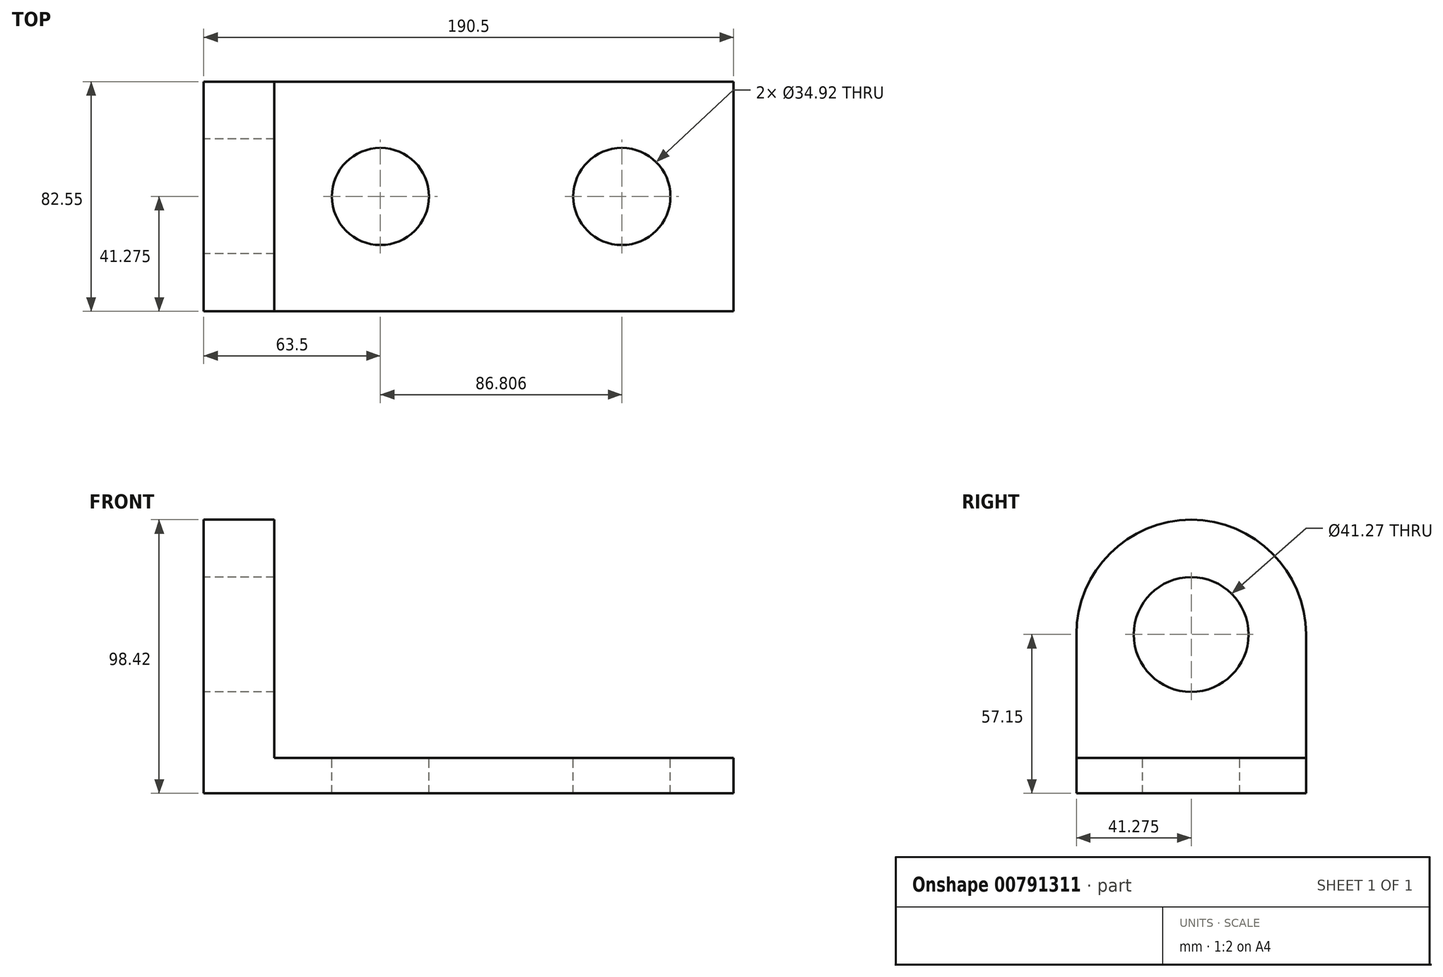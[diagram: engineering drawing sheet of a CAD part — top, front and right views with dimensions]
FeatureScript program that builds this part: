
annotation { "Feature Type Name" : "Feature", "Feature Type Description" : "" }
export const myFeature = defineFeature(function(context is Context, id is Id, definition is map)
    precondition{}
    {
        {
            var Q0;
            Q0=qCreatedBy(makeId("Front.planeOp"),FACE);
            var sketch = newSketch(context, id + "F0", { "sketchPlane" : qUnion([Q0])});
            skLineSegment(sketch, "E0", {"start": v(0, 0) * mm, "end": v(190.5, 0) * mm});
            skLineSegment(sketch, "E1", {"start": v(190.5, 0) * mm, "end": v(190.5, 12.7) * mm});
            skLineSegment(sketch, "E2", {"start": v(190.5, 12.7) * mm, "end": v(25.4, 12.7) * mm});
            skLineSegment(sketch, "E3", {"start": v(0, 0) * mm, "end": v(0, 107.95) * mm});
            skLineSegment(sketch, "E4", {"start": v(0, 107.95) * mm, "end": v(25.4, 107.95) * mm});
            skLineSegment(sketch, "E5", {"start": v(25.4, 12.7) * mm, "end": v(25.4, 107.95) * mm});
            skSolve(sketch);
        }
        {
            var Q0;
            Q0=makeQuery(id+"F0.imprint","IMPRINT",FACE,{"disambiguationData":[TD([[makeQuery(id+"F0.imprint","IMPRINT",EDGE,{"derivedFrom":sQuery(id+"F0.wireOp",EDGE,"E0")}),1.0]])]});
            extrude(context, id + "F1", {"entities" : qUnion([Q0]), "depth" : 82.55 * mm, "offsetDistance" : 25.4 * mm});
        }
        {
            var Q0;
            Q0=makeQuery(id+"F1.opExtrude","SWEPT_FACE",FACE,{"disambiguationData":[OSD([sQuery(id+"F0.wireOp",EDGE,"E2")])]});
            var sketch = newSketch(context, id + "F2", { "sketchPlane" : qUnion([Q0])});
            skLineSegment(sketch, "E6", {"start": v(25.4, -41.28) * mm, "end": v(63.5, -41.28) * mm, "construction": true});
            skLineSegment(sketch, "E7", {"start": v(63.5, -41.28) * mm, "end": v(150.3, -41.28) * mm, "construction": true});
            skCircle(sketch, "E8", {"center": v(63.5, -41.28) * mm, "radius": 17.46 * mm});
            skCircle(sketch, "E9", {"center": v(150.3, -41.28) * mm, "radius": 17.46 * mm});
            skSolve(sketch);
        }
        {
            var Q0;
            Q0=makeQuery(id+"F2.imprint","IMPRINT",FACE,{"disambiguationData":[TD([[makeQuery(id+"F2.imprint","IMPRINT",EDGE,{"derivedFrom":sQuery(id+"F2.wireOp",EDGE,"E8")}),1.0]])]});
            var Q1;
            Q1=makeQuery(id+"F2.imprint","IMPRINT",FACE,{"disambiguationData":[TD([[makeQuery(id+"F2.imprint","IMPRINT",EDGE,{"derivedFrom":sQuery(id+"F2.wireOp",EDGE,"E9")}),1.0]])]});
            extrude(context, id + "F3", {"entities" : qUnion([Q0, Q1]), "operationType" : NewBodyOperationType.REMOVE, "oppositeDirection" : true, "depth" : 25.4 * mm, "offsetDistance" : 25.4 * mm});
        }
        {
            var Q0;
            Q0=makeQuery(id+"F1.opExtrude","SWEPT_FACE",FACE,{"disambiguationData":[OSD([sQuery(id+"F0.wireOp",EDGE,"E3")])]});
            var sketch = newSketch(context, id + "F4", { "sketchPlane" : qUnion([Q0])});
            skLineSegment(sketch, "E10", {"start": v(0, 0) * mm, "end": v(0, 57.15) * mm, "construction": true});
            skLineSegment(sketch, "E11", {"start": v(82.55, 0) * mm, "end": v(82.55, 57.15) * mm, "construction": true});
            skArc(sketch, "E12", {"start": v(82.55, 57.15) * mm, "mid": v(41.28, 98.42) * mm, "end": v(0, 57.15) * mm});
            skSolve(sketch);
        }
        {
            var Q0;
            {var subQ0=sQuery(id+"F4.wireOp",EDGE,"E12");Q0=makeQuery(id+"F4.imprint","IMPRINT",FACE,{"disambiguationData":[TD([[makeQuery(id+"F4.imprint","IMPRINT",EDGE,{"derivedFrom":subQ0}),-1.0]])]});}
            extrude(context, id + "F5", {"entities" : qUnion([Q0]), "operationType" : NewBodyOperationType.REMOVE, "oppositeDirection" : true, "depth" : 25.4 * mm, "offsetDistance" : 25.4 * mm});
        }
        {
            var Q0;
            Q0=makeQuery(id+"F1.opExtrude","SWEPT_FACE",FACE,{"disambiguationData":[OSD([sQuery(id+"F0.wireOp",EDGE,"E3")])]});
            var sketch = newSketch(context, id + "F6", { "sketchPlane" : qUnion([Q0])});
            skLineSegment(sketch, "E13", {"start": v(41.28, 0) * mm, "end": v(41.28, 57.15) * mm, "construction": true});
            skCircle(sketch, "E14", {"center": v(41.28, 57.15) * mm, "radius": 20.64 * mm});
            skSolve(sketch);
        }
        {
            var Q0;
            Q0=makeQuery(id+"F6.imprint","IMPRINT",FACE,{"disambiguationData":[TD([[makeQuery(id+"F6.imprint","IMPRINT",EDGE,{"derivedFrom":sQuery(id+"F6.wireOp",EDGE,"E14")}),1.0]])]});
            extrude(context, id + "F7", {"entities" : qUnion([Q0]), "operationType" : NewBodyOperationType.REMOVE, "endBound" : BoundingType.UP_TO_NEXT, "oppositeDirection" : true, "depth" : 25.4 * mm, "offsetDistance" : 25.4 * mm});
        }
    });
